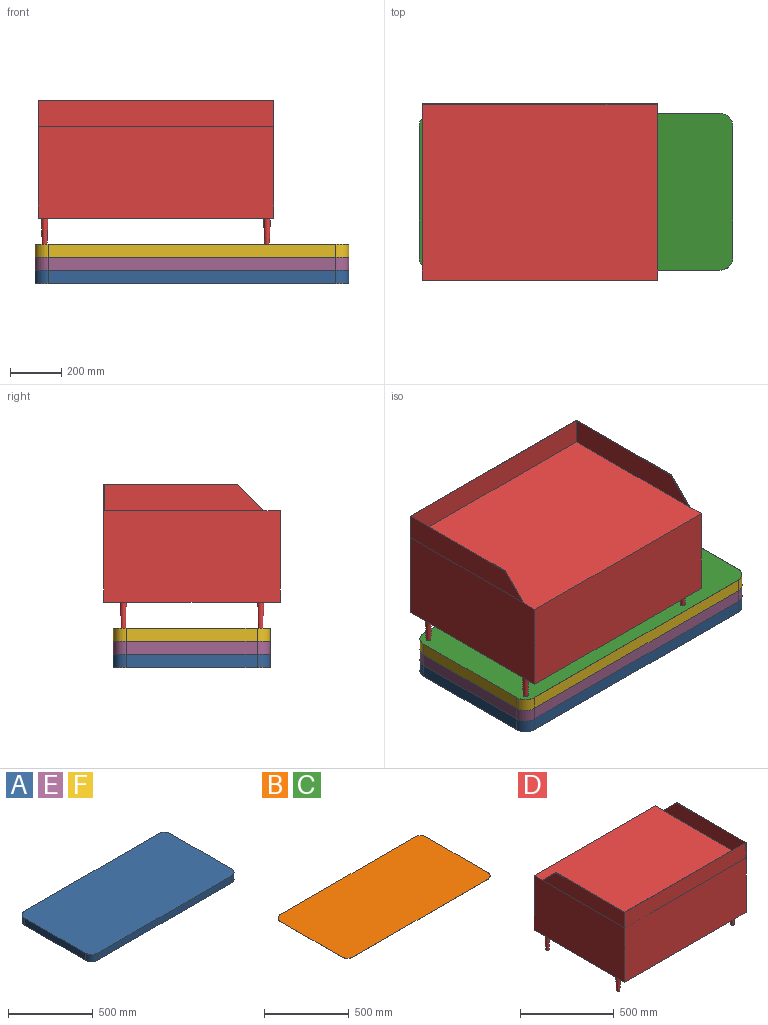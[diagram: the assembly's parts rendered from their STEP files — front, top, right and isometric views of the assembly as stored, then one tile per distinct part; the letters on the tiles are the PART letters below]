
ASSEMBLY  parts=6 mates=2
PART A: 10 faces, bbox 1219.2x609.6x50.8 mm
  f0: plane 508x50.8mm, normal (1,0,0), area 25806.4mm2, adj f1,f7,f8,f9
  f1: cylinder r=50.8mm len=50.8mm, axis (0,0,1), area 4053.7mm2, adj f0,f2,f8,f9
  f2: plane 1117.6x50.8mm, normal (0,1,0), area 56774.1mm2, adj f1,f3,f8,f9
  f3: cylinder r=50.8mm len=50.8mm, axis (0,0,1), area 4053.7mm2, adj f2,f4,f8,f9
  f4: plane 508x50.8mm, normal (-1,0,0), area 25806.4mm2, adj f3,f5,f8,f9
  f5: cylinder r=50.8mm len=50.8mm, axis (0,0,1), area 4053.7mm2, adj f4,f6,f8,f9
  f6: plane 1117.6x50.8mm, normal (0,-1,0), area 56774.1mm2, adj f5,f7,f8,f9
  f7: cylinder r=50.8mm len=50.8mm, axis (0,0,1), area 4053.7mm2, adj f0,f6,f8,f9
  f8: plane 1219.2x609.6mm, normal (0,0,-1), area 741009.1mm2, adj f0,f1,f2,f3,f4,f5,f6,f7
  f9: plane 1219.2x609.6mm, normal (0,0,1), area 741009.1mm2, adj f0,f1,f2,f3,f4,f5,f6,f7
PART B: 10 faces, bbox 1219.2x609.6x0.6 mm
  f0: plane 508x0.61mm, normal (1,0,0), area 309.7mm2, adj f1,f7,f8,f9
  f1: cylinder r=50.8mm len=50.8mm, axis (0,0,-1), area 48.6mm2, adj f0,f2,f8,f9
  f2: plane 1117.6x0.61mm, normal (0,1,0), area 681.3mm2, adj f1,f3,f8,f9
  f3: cylinder r=50.8mm len=50.8mm, axis (0,0,-1), area 48.6mm2, adj f2,f4,f8,f9
  f4: plane 508x0.61mm, normal (-1,0,0), area 309.7mm2, adj f3,f5,f8,f9
  f5: cylinder r=50.8mm len=50.8mm, axis (0,0,-1), area 48.6mm2, adj f4,f6,f8,f9
  f6: plane 1117.6x0.61mm, normal (0,-1,0), area 681.3mm2, adj f5,f7,f8,f9
  f7: cylinder r=50.8mm len=50.8mm, axis (0,0,-1), area 48.6mm2, adj f0,f6,f8,f9
  f8: plane 1219.2x609.6mm, normal (0,0,1), area 741009.1mm2, adj f0,f1,f2,f3,f4,f5,f6,f7
  f9: plane 1219.2x609.6mm, normal (0,0,-1), area 741009.1mm2, adj f0,f1,f2,f3,f4,f5,f6,f7
PART C: same geometry as B
PART D: 20 faces, bbox 914.4x685.8x558.8 mm
  f0: plane 914.4x684.23mm, normal (0,0,1), area 623700.5mm2, adj f1,f3,f4,f14,f15,f16,f18,f19
  f1: plane 685.8x457.2mm, normal (-1,0,0), area 301934.9mm2, adj f0,f2,f4,f5,f17,f19
  f2: plane 914.4x457.2mm, normal (0,-1,0), area 418063.7mm2, adj f1,f3,f5,f17
  f3: plane 685.8x457.2mm, normal (1,0,0), area 301934.9mm2, adj f0,f2,f4,f5,f17,f18
  f4: plane 914.4x355.6mm, normal (0,1,0), area 325160.6mm2, adj f0,f1,f3,f5
  f5: plane 914.4x685.8mm, normal (0,0,-1), area 624977.6mm2, adj f1,f2,f3,f4,f6,f8,f10,f12
  f6: cone r=25.4mm half-angle=2deg, axis (0,0,1), area 7159.4mm2, adj f5,f7
  f7: plane 18.87x18.87mm, normal (0,0,-1), area 279.6mm2, adj f6
  f8: cone r=25.4mm half-angle=2deg, axis (0,0,1), area 7159.4mm2, adj f5,f9
  f9: plane 18.87x18.87mm, normal (0,0,-1), area 279.6mm2, adj f8
  f10: cone r=25.4mm half-angle=2deg, axis (0,0,1), area 7159.4mm2, adj f5,f11
  f11: plane 18.87x18.87mm, normal (0,0,-1), area 279.6mm2, adj f10
  f12: cone r=25.4mm half-angle=2deg, axis (0,0,1), area 7159.4mm2, adj f5,f13
  f13: plane 18.87x18.87mm, normal (0,0,-1), area 279.6mm2, adj f12
  f14: plane 620.73x101.6mm, normal (-1,0,0), area 57904.4mm2, adj f0,f15,f17,f18
  f15: plane 911.25x101.6mm, normal (0,1,0), area 92583mm2, adj f0,f14,f16,f17
  f16: plane 620.73x101.6mm, normal (1,0,0), area 57904.4mm2, adj f0,f15,f17,f19
  f17: plane 914.4x520.7mm, normal (0,0,1), area 3075mm2, adj f1,f2,f3,f14,f15,f16,f18,f19
  f18: plane 101.6x101.6mm, normal (0,0.71,0.71), area 226.3mm2, adj f0,f3,f14,f17
  f19: plane 101.6x101.6mm, normal (0,0.71,0.71), area 226.3mm2, adj f0,f1,f16,f17
PART E: same geometry as A
PART F: same geometry as A
PLACE A rot(axis=(0,0,-1),180deg) t=(1168.4,495.3,0)mm
PLACE B rot(axis=(0,0,-1),180deg) t=(1168.4,495.3,-50.8)mm
PLACE C rot(axis=(0,0,-1),180deg) t=(1168.4,495.3,102.21)mm
PLACE D rot(axis=(0,0,-1),180deg) t=(-7966.46,3124.58,559.41)mm
PLACE E rot(axis=(0,0,-1),180deg) t=(1168.4,495.3,50.8)mm
PLACE F rot(axis=(0,0,-1),180deg) t=(1168.4,495.3,101.6)mm
MATE planar B.f8 <-> A.f8  axis (0,0,1) through (584.2,247.65,-50.19)mm
MATE planar C.f9 <-> F.f9  axis (0,0,-1) through (584.2,247.65,102.21)mm
